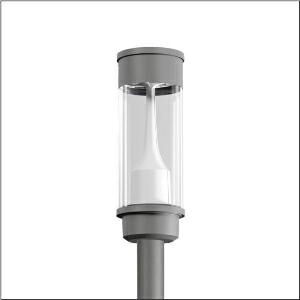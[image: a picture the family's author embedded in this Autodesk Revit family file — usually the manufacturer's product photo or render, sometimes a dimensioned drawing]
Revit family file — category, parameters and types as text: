
# Revit family: litepole_iq___p1_0a_5xa5415ff14h_1a61
name_source: partatom
category: Lighting Fixtures
units: mm (PartAtom-declared; Revit-internal decimal feet)

## family parameters
Cut with Voids When Loaded = No
Host = Face
Light Source = No
Part Type = Normal
Room Calculation Point = No
Round Connector Dimension = Use Diameter
Shared = No

## types (1)
- --- (1 x LED, 1510 lm, 10.5 W, 3000K)
    Apparent Load = 11 VA
    CIE Flux Codes = 32 61 90 93 100
    Color Rendering = 70
    Color Temperature = 3000K
    Default Elevation = 1800 mm
    Description = Litepole iQ, mast luminaire, Module 540 iQ-SR, primary light control with 3 zone facetted reflector, of plastic, silver coated, highly specular, structured, primary optical cover: cover, of PMMA, transparent, light distribution: P1.0a, light emission: direct distribution, primary light characteristic: strongly asymmetric, installation type: post-top, LED, High Power LED, rated luminous flux: 1.510lm, luminous efficacy: 144lm/W, light colour: 730, colour temperature: 3000K, control gear: ECG iQ, control: Auto-Match, Temp-Guard, Lumen-Switch, Night-Set, Smart-Wire, Light-Fading, Desk-Remote (wireless, voltage-free reading and setting of iQ features in the workshop via application-optimized NFC function/RFID function), optimised constant luminous flux control (CLO 2.0), Street-Remote, presetting dimming logarithmic, with terminal, 6-pole, max. 2.5mm², mains connection: 230..240V, AC, 50/60Hz, start of lifetime: 11W, end of service life: 11W, reduction: 5W, luminaire housing, upper part, of glass-fibre reinforced polyester, coated, Siteco® metallic grey (DB 702S), diameter: 210mm, height: 590mm, spigot size: d x l = 76 x 70mm (post-top) | with reducer (optional accessory) 60 x 70mm, post-top mast mounting element, of diecast aluminium, coated, Siteco® metallic grey (DB 702S), Module 540 iQ-SR, traffic white (RAL 9016), equipment: standard, protection rating (complete): IP65, insulation class (complete): insulation class II (safety insulation), certification: CE, ENEC, VDE, packaging unit: 1 piece

Light Distribution: P1.0a
    Height = 590 mm
    Lamp = 1 x LED
    Lamp Light Flux = 1510 lm
    Lamp Power = 10.5 W
    Lamp count = 1
    Length = 220 mm
    Luminous efficacy = 144 lm/W
    Manufacturer = Siteco
    ModVariant = No
    Model = 5XA5415FF14H
    Number of Poles = 1
    OnlyDefault = Yes
    Power Factor = 1
    Product Name = Litepole iQ | P1.0a
    Product group = mast luminaire | pylon top
    ProductGroupID = 6100
    Protection Class = Protection class II
    Protection Degree = IP 65
    RLX_Detail_Level = 1
    RLX_Emergency_Light_Flux = 0 lm
    RLX_Emergency_Type = 0
    RLX_Emergency_Type_DB = No
    RlxData = <blob elided: 63729 chars, md5=430aba91>
    Socket = socket
    Standby Power = 0 W
    System Light Flux = 1510 lm
    System Power = 11 W
    Type Comments = factory setting: luminous flux: 100 % | dim-lin: 254 | 419 mA
    Type Image = l_1006025.jpg
    URL = http://relux.com
    VarID = @adj_108905
    Voltage = 0 V
    Weight = 0.00 kg
    Width = 0 mm  [stored 0 ft]

note: [stored X ft] marks values corroborated as IEEE doubles in the binary element streams (Revit-internal decimal feet)

## geometry (parser evidence)
native form markers: Blend x4, Sweep x13
no freeform markers — native parametric forms only
